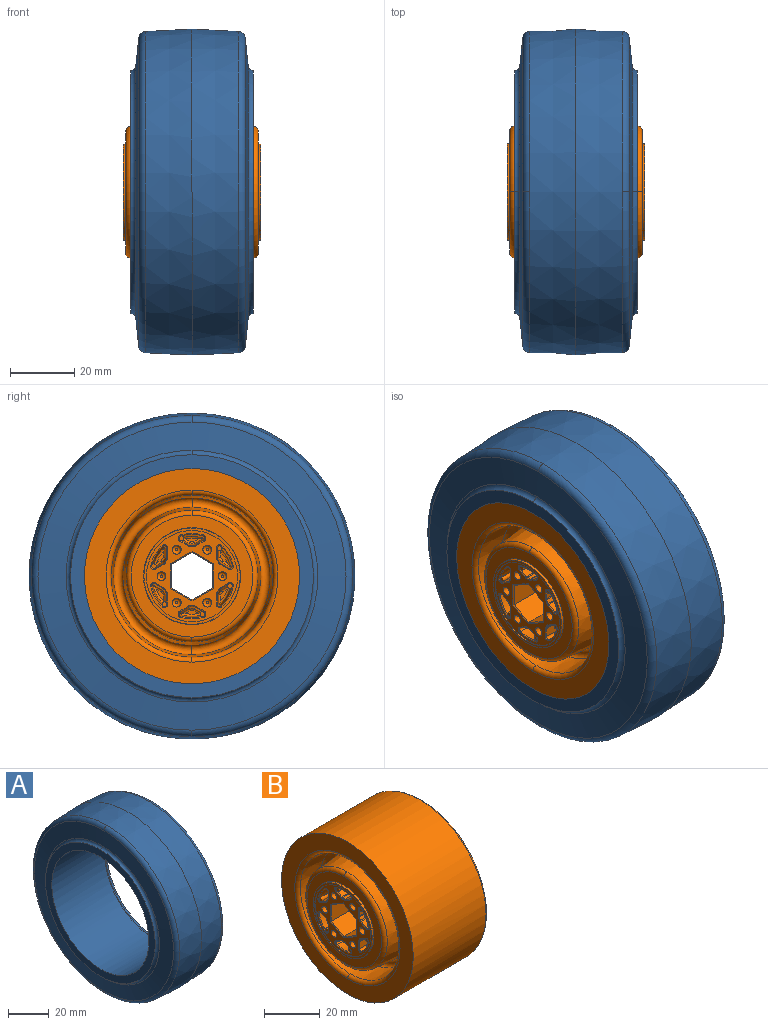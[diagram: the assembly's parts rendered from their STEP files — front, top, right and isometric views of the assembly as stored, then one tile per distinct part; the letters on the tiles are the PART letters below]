
ASSEMBLY  parts=2 mates=1
PART A: 18 faces, bbox 40.3x108.3x108.3 mm
  f0: torus R=47.76mm, axis (-1,0,0), area 500.4mm2, adj f1,f2,f9
  f1: torus R=47.76mm, axis (-1,0,0), area 500.4mm2, adj f0,f2,f9
  f2: cone r=48mm half-angle=84deg, axis (-1,0,0), area 2420.9mm2, adj f0,f1,f3,f4
  f3: torus R=39.37mm, axis (-1,0,0), area 269.1mm2, adj f2,f4,f5
  f4: torus R=39.37mm, axis (-1,0,0), area 269.1mm2, adj f2,f3,f5
  f5: plane 75.69x75.69mm, normal (1,0,0), area 968.2mm2, adj f3,f4,f6
  f6: cone r=33.86mm half-angle=3deg, axis (-1,0,0), area 305mm2, adj f5,f7,f8
  f7: torus R=32.08mm, axis (-1,0,0), area 43.2mm2, adj f6,f8,f17
  f8: torus R=32.08mm, axis (-1,0,0), area 43.2mm2, adj f6,f7,f17
  f9: cone r=50.8mm half-angle=3deg, axis (-1,0,0), area 4586.3mm2, adj f0,f1,f10
  f10: cone r=50.8mm half-angle=3deg, axis (1,0,0), area 4586.3mm2, adj f9,f11,f12
  f11: torus R=47.76mm, axis (-1,0,0), area 500.4mm2, adj f10,f12,f13
  f12: torus R=47.76mm, axis (-1,0,0), area 500.4mm2, adj f10,f11,f13
  f13: cone r=48mm half-angle=84deg, axis (1,0,0), area 2420.9mm2, adj f11,f12,f14,f15
  f14: torus R=39.37mm, axis (-1,0,0), area 269.1mm2, adj f13,f15,f16
  f15: torus R=39.37mm, axis (-1,0,0), area 269.1mm2, adj f13,f14,f16
  f16: plane 75.69x75.69mm, normal (-1,0,0), area 968.2mm2, adj f14,f15,f17
  f17: cylinder r=33.53mm len=67.06mm, axis (1,0,0), area 7806.5mm2, adj f7,f8,f16
PART B: 401 faces, bbox 44.4x74.2x74.2 mm
  f0: torus R=32.08mm, axis (-1,0,0), area 197mm2, adj f2,f57,f400
  f1: plane 67.06x67.06mm, normal (-1,0,0), area 1275.7mm2, adj f10,f56,f400
  f2: torus R=32.08mm, axis (-1,0,0), area 197mm2, adj f0,f57,f400
  f3: revolved ~0.32x0.17mm, area 0.1mm2, adj f41,f43,f102,f103
  f4: revolved ~0.32x0.17mm, area 0.1mm2, adj f42,f48,f86,f87
  f5: torus R=18.98mm, axis (-1,0,0), area 141.5mm2, adj f44,f49,f51
  f6: torus R=18.98mm, axis (-1,0,0), area 141.5mm2, adj f45,f50,f52
  f7: torus R=22.96mm, axis (-1,0,0), area 326.1mm2, adj f44,f46,f53
  f8: torus R=22.96mm, axis (-1,0,0), area 326.1mm2, adj f45,f47,f54
  f9: torus R=26.8mm, axis (-1,0,0), area 183.7mm2, adj f46,f55,f57
  f10: torus R=26.8mm, axis (-1,0,0), area 183.7mm2, adj f1,f47,f56
  f11: cone r=14.2mm half-angle=0.5deg, axis (1,0,0), area 26.8mm2, adj f118,f119
  f12: cylinder r=1.38mm len=18.65mm, axis (1,0,0), area 161.1mm2, adj f19,f119
  f13: cylinder r=1.38mm len=18.65mm, axis (1,0,0), area 161.1mm2, adj f20,f119
  f14: cylinder r=1.38mm len=18.65mm, axis (1,0,0), area 161.1mm2, adj f21,f119
  f15: cylinder r=1.38mm len=18.65mm, axis (1,0,0), area 161.1mm2, adj f22,f119
  f16: cylinder r=1.38mm len=18.65mm, axis (1,0,0), area 161.1mm2, adj f23,f119
  f17: cylinder r=1.38mm len=18.65mm, axis (1,0,0), area 161.1mm2, adj f24,f119
  f18: cone r=13.01mm half-angle=1.5deg, axis (1,0,0), area 128.2mm2, adj f121,f174,f175,f209
  f19: torus R=0.38mm, axis (1,0,0), area 10mm2, adj f12,f239
  f20: torus R=0.38mm, axis (1,0,0), area 10mm2, adj f13,f240
  f21: torus R=0.38mm, axis (1,0,0), area 10mm2, adj f14,f241
  f22: torus R=0.38mm, axis (1,0,0), area 10mm2, adj f15,f242
  f23: torus R=0.38mm, axis (1,0,0), area 10mm2, adj f16,f243
  f24: torus R=0.38mm, axis (1,0,0), area 10mm2, adj f17,f244
  f25: cone r=10.06mm half-angle=1.5deg, axis (-1,0,0), area 23.4mm2, adj f149,f225,f228,f262
  f26: cone r=14.2mm half-angle=0.5deg, axis (-1,0,0), area 26.8mm2, adj f251,f269
  f27: cylinder r=1.38mm len=18.65mm, axis (-1,0,0), area 161.1mm2, adj f34,f269
  f28: cylinder r=1.38mm len=18.65mm, axis (-1,0,0), area 161.1mm2, adj f35,f269
  f29: cylinder r=1.38mm len=18.65mm, axis (-1,0,0), area 161.1mm2, adj f36,f269
  f30: cylinder r=1.38mm len=18.65mm, axis (-1,0,0), area 161.1mm2, adj f37,f269
  f31: cylinder r=1.38mm len=18.65mm, axis (-1,0,0), area 161.1mm2, adj f38,f269
  f32: cylinder r=1.38mm len=18.65mm, axis (-1,0,0), area 161.1mm2, adj f39,f269
  f33: cone r=13.01mm half-angle=1.5deg, axis (-1,0,0), area 128.2mm2, adj f311,f343,f344,f372
  f34: torus R=0.38mm, axis (-1,0,0), area 10mm2, adj f27,f377
  f35: torus R=0.38mm, axis (-1,0,0), area 10mm2, adj f28,f378
  f36: torus R=0.38mm, axis (-1,0,0), area 10mm2, adj f29,f379
  f37: torus R=0.38mm, axis (-1,0,0), area 10mm2, adj f30,f380
  f38: torus R=0.38mm, axis (-1,0,0), area 10mm2, adj f31,f381
  f39: torus R=0.38mm, axis (-1,0,0), area 10mm2, adj f32,f382
  f40: cone r=10.06mm half-angle=1.5deg, axis (1,0,0), area 23.4mm2, adj f293,f357,f360,f389
  f41: cone r=15.17mm half-angle=0.5deg, axis (-1,0,0), area 1115.7mm2, adj f3,f43,f88,f89,f90,f91,f92,f93
  f42: cone r=15.17mm half-angle=0.5deg, axis (1,0,0), area 1115.7mm2, adj f4,f48,f58,f59,f60,f61,f62,f63
  f43: cylinder r=15.11mm len=30.21mm, axis (-1,0,0), area 1052.5mm2, adj f3,f41,f49,f88,f89,f90,f91,f92
  f44: cone r=21.44mm half-angle=5deg, axis (-1,0,0), area 1421mm2, adj f5,f7,f51,f53
  f45: cone r=21.44mm half-angle=5deg, axis (1,0,0), area 1421mm2, adj f6,f8,f52,f54
  f46: cone r=25.28mm half-angle=5deg, axis (1,0,0), area 1436.6mm2, adj f7,f9,f53,f55
  f47: cone r=25.28mm half-angle=5deg, axis (-1,0,0), area 1436.6mm2, adj f8,f10,f54,f56
  f48: cylinder r=15.11mm len=30.21mm, axis (-1,0,0), area 1052.4mm2, adj f4,f42,f50,f58,f59,f60,f61,f62
  f49: plane 37.97x37.97mm, normal (1,0,0), area 415.1mm2, adj f5,f43,f51
  f50: plane 37.97x37.97mm, normal (-1,0,0), area 415.1mm2, adj f6,f48,f52
  f51: torus R=18.98mm, axis (-1,0,0), area 141.5mm2, adj f5,f44,f49
  f52: torus R=18.98mm, axis (-1,0,0), area 141.5mm2, adj f6,f45,f50
  f53: torus R=22.96mm, axis (-1,0,0), area 326.1mm2, adj f7,f44,f46
  f54: torus R=22.96mm, axis (-1,0,0), area 326.1mm2, adj f8,f45,f47
  f55: torus R=26.8mm, axis (-1,0,0), area 183.7mm2, adj f9,f46,f57
  f56: torus R=26.8mm, axis (-1,0,0), area 183.7mm2, adj f1,f10,f47
  f57: plane 64.16x64.16mm, normal (1,0,0), area 977.6mm2, adj f0,f2,f9,f55
  f58: torus R=15.35mm, axis (-1,0,0), area 0.1mm2, adj f42,f48,f59,f83
  f59: bspline ~0.78x0.62mm, area 0.2mm2, adj f42,f48,f58,f82
  f60: torus R=15.35mm, axis (-1,0,0), area 0.1mm2, adj f42,f48,f61,f70
  f61: bspline ~0.78x0.62mm, area 0.2mm2, adj f42,f48,f60,f69
  f62: bspline ~0.78x0.71mm, area 0.1mm2, adj f42,f48,f63,f87
  f63: extruded ~5.58x0.2mm, area 0.6mm2, adj f42,f48,f62
  f64: extruded ~5.58x0.17mm, area 0.6mm2, adj f42,f48,f65
  f65: bspline ~0.78x0.6mm, area 0.2mm2, adj f42,f48,f64,f66
  f66: torus R=15.35mm, axis (-1,0,0), area 0.1mm2, adj f42,f48,f65,f67
  f67: bspline ~0.78x0.63mm, area 0.1mm2, adj f42,f48,f66,f68
  f68: extruded ~5.58x0.18mm, area 0.6mm2, adj f42,f48,f67
  f69: extruded ~5.58x0.18mm, area 0.6mm2, adj f42,f48,f61
  f70: bspline ~0.78x0.6mm, area 0.1mm2, adj f42,f48,f60,f71
  f71: extruded ~5.58x0.17mm, area 0.6mm2, adj f42,f48,f70
  f72: extruded ~5.58x0.2mm, area 0.6mm2, adj f42,f48,f73
  f73: bspline ~0.78x0.71mm, area 0.2mm2, adj f42,f48,f72,f74
  f74: torus R=15.35mm, axis (-1,0,0), area 0.1mm2, adj f42,f48,f73,f75
  f75: bspline ~0.78x0.71mm, area 0.1mm2, adj f42,f48,f74,f76
  f76: extruded ~5.58x0.2mm, area 0.6mm2, adj f42,f48,f75
  f77: extruded ~5.58x0.17mm, area 0.6mm2, adj f42,f48,f78
  f78: bspline ~0.78x0.6mm, area 0.2mm2, adj f42,f48,f77,f79
  f79: torus R=15.35mm, axis (-1,0,0), area 0.1mm2, adj f42,f48,f78,f80
  f80: bspline ~0.78x0.63mm, area 0.2mm2, adj f42,f48,f79,f81
  f81: extruded ~5.58x0.18mm, area 0.6mm2, adj f42,f48,f80
  f82: extruded ~5.58x0.18mm, area 0.6mm2, adj f42,f48,f59
  f83: bspline ~0.78x0.6mm, area 0.1mm2, adj f42,f48,f58,f84
  f84: extruded ~5.58x0.17mm, area 0.6mm2, adj f42,f48,f83
  f85: extruded ~5.58x0.2mm, area 0.6mm2, adj f42,f48,f86
  f86: bspline ~0.78x0.71mm, area 0.2mm2, adj f4,f42,f48,f85
  f87: revolved ~0.32x0.17mm, area 0.1mm2, adj f4,f42,f48,f62
  f88: bspline ~0.78x0.71mm, area 0.1mm2, adj f41,f43,f89,f117
  f89: extruded ~5.58x0.2mm, area 0.6mm2, adj f41,f43,f88
  f90: extruded ~5.58x0.17mm, area 0.6mm2, adj f41,f43,f91
  f91: bspline ~0.78x0.6mm, area 0.2mm2, adj f41,f43,f90,f92
  f92: revolved ~0.59x0.37mm, area 0.1mm2, adj f41,f43,f91,f93
  f93: bspline ~0.78x0.63mm, area 0.2mm2, adj f41,f43,f92,f94
  f94: extruded ~5.58x0.18mm, area 0.6mm2, adj f41,f43,f93
  f95: extruded ~5.58x0.18mm, area 0.6mm2, adj f41,f43,f96
  f96: bspline ~0.78x0.62mm, area 0.2mm2, adj f41,f43,f95,f97
  f97: torus R=15.35mm, axis (-1,0,0), area 0.1mm2, adj f41,f43,f96,f98
  f98: bspline ~0.78x0.6mm, area 0.1mm2, adj f41,f43,f97,f99
  f99: extruded ~5.58x0.17mm, area 0.6mm2, adj f41,f43,f98
  f100: extruded ~5.58x0.2mm, area 0.6mm2, adj f41,f43,f101
  f101: bspline ~0.78x0.71mm, area 0.2mm2, adj f41,f43,f100,f102
  f102: revolved ~0.32x0.17mm, area 0.1mm2, adj f3,f41,f43,f101
  f103: bspline ~0.78x0.71mm, area 0.1mm2, adj f3,f41,f43,f104
  f104: extruded ~5.58x0.2mm, area 0.6mm2, adj f41,f43,f103
  f105: extruded ~5.58x0.17mm, area 0.6mm2, adj f41,f43,f106
  f106: bspline ~0.78x0.6mm, area 0.2mm2, adj f41,f43,f105,f107
  f107: torus R=15.35mm, axis (-1,0,0), area 0.1mm2, adj f41,f43,f106,f108
  f108: bspline ~0.78x0.63mm, area 0.1mm2, adj f41,f43,f107,f109
  f109: extruded ~5.58x0.18mm, area 0.6mm2, adj f41,f43,f108
  f110: extruded ~5.58x0.18mm, area 0.6mm2, adj f41,f43,f111
  f111: bspline ~0.78x0.63mm, area 0.2mm2, adj f41,f43,f110,f112
  f112: torus R=15.35mm, axis (-1,0,0), area 0.1mm2, adj f41,f43,f111,f113
  f113: bspline ~0.78x0.6mm, area 0.1mm2, adj f41,f43,f112,f114
  f114: extruded ~5.58x0.17mm, area 0.6mm2, adj f41,f43,f113
  f115: extruded ~5.58x0.2mm, area 0.6mm2, adj f41,f43,f116
  f116: bspline ~0.78x0.71mm, area 0.2mm2, adj f41,f43,f115,f117
  f117: torus R=15.35mm, axis (-1,0,0), area 0.1mm2, adj f41,f43,f88,f116
  f118: plane 29.99x29.99mm, normal (1,0,0), area 72.9mm2, adj f11,f41
  f119: plane 28.52x28.52mm, normal (1,0,0), area 288.3mm2, adj f11,f12,f13,f14,f15,f16,f17,f120
  f120: bspline ~2.05x0.93mm, area 1mm2, adj f119,f121,f127,f174
  f121: torus R=13.31mm, axis (1,0,0), area 3.3mm2, adj f18,f119,f120,f122
  f122: bspline ~2.04x0.95mm, area 1mm2, adj f119,f121,f123,f175
  f123: cylinder r=0.3mm len=2.75mm, axis (0,0.87,-0.5), area 1.4mm2, adj f119,f122,f124,f176
  f124: bspline ~0.74x0.49mm, area 0.3mm2, adj f119,f123,f125,f210
  f125: torus R=9.28mm, axis (1,0,0), area 0.6mm2, adj f119,f124,f126,f253
  f126: bspline ~0.72x0.49mm, area 0.3mm2, adj f119,f125,f127,f213
  f127: cylinder r=0.3mm len=2.75mm, axis (0,0.87,0.5), area 1.4mm2, adj f119,f120,f126,f177
  f128: bspline ~1.72x1.42mm, area 1mm2, adj f119,f129,f135,f178
  f129: torus R=13.31mm, axis (1,0,0), area 3.3mm2, adj f119,f128,f130,f179
  f130: bspline ~1.92x1.14mm, area 1mm2, adj f119,f129,f131,f180
  f131: cylinder r=0.3mm len=3mm, axis (0,0,-1), area 1.4mm2, adj f119,f130,f132,f181
  f132: bspline ~0.73x0.52mm, area 0.3mm2, adj f119,f131,f133,f215
  f133: torus R=9.28mm, axis (1,0,0), area 0.6mm2, adj f119,f132,f134,f256
  f134: bspline ~0.7x0.68mm, area 0.3mm2, adj f119,f133,f135,f218
  f135: cylinder r=0.3mm len=2.75mm, axis (0,0.87,-0.5), area 1.4mm2, adj f119,f128,f134,f182
  f136: bspline ~1.9x1.15mm, area 1mm2, adj f119,f137,f143,f183
  f137: torus R=13.31mm, axis (1,0,0), area 3.3mm2, adj f119,f136,f138,f184
  f138: bspline ~1.69x1.45mm, area 1mm2, adj f119,f137,f139,f185
  f139: cylinder r=0.3mm len=2.75mm, axis (0,-0.87,-0.5), area 1.4mm2, adj f119,f138,f140,f186
  f140: bspline ~0.7x0.68mm, area 0.3mm2, adj f119,f139,f141,f220
  f141: torus R=9.28mm, axis (1,0,0), area 0.6mm2, adj f119,f140,f142,f259
  f142: bspline ~0.73x0.51mm, area 0.3mm2, adj f119,f141,f143,f223
  f143: cylinder r=0.3mm len=3mm, axis (0,0,-1), area 1.4mm2, adj f119,f136,f142,f187
  f144: bspline ~2.05x0.93mm, area 1mm2, adj f119,f145,f151,f188
  f145: torus R=13.31mm, axis (1,0,0), area 3.3mm2, adj f119,f144,f146,f189
  f146: bspline ~2.04x0.95mm, area 1mm2, adj f119,f145,f147,f190
  f147: cylinder r=0.3mm len=2.75mm, axis (0,-0.87,0.5), area 1.4mm2, adj f119,f146,f148,f191
  f148: bspline ~0.74x0.49mm, area 0.3mm2, adj f119,f147,f149,f225
  f149: torus R=9.28mm, axis (1,0,0), area 0.6mm2, adj f25,f119,f148,f150
  f150: bspline ~0.72x0.49mm, area 0.3mm2, adj f119,f149,f151,f228
  f151: cylinder r=0.3mm len=2.75mm, axis (0,-0.87,-0.5), area 1.4mm2, adj f119,f144,f150,f192
  f152: bspline ~1.72x1.42mm, area 1mm2, adj f119,f153,f159,f193
  f153: torus R=13.31mm, axis (1,0,0), area 3.3mm2, adj f119,f152,f154,f194
  f154: bspline ~1.92x1.14mm, area 1mm2, adj f119,f153,f155,f195
  f155: cylinder r=0.3mm len=3mm, axis (0,0,1), area 1.4mm2, adj f119,f154,f156,f196
  f156: bspline ~0.73x0.52mm, area 0.3mm2, adj f119,f155,f157,f230
  f157: torus R=9.28mm, axis (1,0,0), area 0.6mm2, adj f119,f156,f158,f264
  f158: bspline ~0.7x0.68mm, area 0.3mm2, adj f119,f157,f159,f233
  f159: cylinder r=0.3mm len=2.75mm, axis (0,-0.87,0.5), area 1.4mm2, adj f119,f152,f158,f197
  f160: bspline ~1.9x1.15mm, area 1mm2, adj f119,f161,f167,f198
  f161: torus R=13.31mm, axis (1,0,0), area 3.3mm2, adj f119,f160,f162,f199
  f162: bspline ~1.69x1.45mm, area 1mm2, adj f119,f161,f163,f200
  f163: cylinder r=0.3mm len=2.75mm, axis (0,0.87,0.5), area 1.4mm2, adj f119,f162,f164,f201
  f164: bspline ~0.7x0.68mm, area 0.3mm2, adj f119,f163,f165,f235
  f165: torus R=9.28mm, axis (1,0,0), area 0.6mm2, adj f119,f164,f166,f267
  f166: bspline ~0.73x0.51mm, area 0.3mm2, adj f119,f165,f167,f238
  f167: cylinder r=0.3mm len=3mm, axis (0,0,1), area 1.4mm2, adj f119,f160,f166,f202
  f168: plane 6.66x4.02mm, normal (0.71,0.35,-0.61), area 3.2mm2, adj f119,f169,f173,f203
  f169: plane 7.69x0.3mm, normal (0.71,0.71,0), area 3.2mm2, adj f119,f168,f170,f204
  f170: plane 6.66x4.02mm, normal (0.71,0.35,0.61), area 3.2mm2, adj f119,f169,f171,f205
  f171: plane 6.66x4.02mm, normal (0.71,-0.35,0.61), area 3.2mm2, adj f119,f170,f172,f206
  f172: plane 7.69x0.3mm, normal (0.71,-0.71,0), area 3.2mm2, adj f119,f171,f173,f207
  f173: plane 6.66x4.02mm, normal (0.71,-0.35,-0.61), area 3.2mm2, adj f119,f168,f172,f208
  f174: revolved ~19.11x1.39mm, area 22.6mm2, adj f18,f120,f177,f209,f212
  f175: revolved ~19.11x1.39mm, area 22.6mm2, adj f18,f122,f176,f209,f211
  f176: plane 18.67x2.84mm, normal (0.03,-0.5,-0.87), area 56mm2, adj f123,f175,f210,f211
  f177: plane 18.67x2.84mm, normal (0.03,0.5,-0.87), area 56mm2, adj f127,f174,f212,f213
  f178: revolved ~19.11x1.14mm, area 22.6mm2, adj f128,f179,f182,f214,f217
  f179: cone r=13.01mm half-angle=1.5deg, axis (1,0,0), area 128.2mm2, adj f129,f178,f180,f214
  f180: revolved ~19.11x1.29mm, area 22.6mm2, adj f130,f179,f181,f214,f216
  f181: plane 18.67x3mm, normal (0.03,-1,0), area 56mm2, adj f131,f180,f215,f216
  f182: plane 18.67x2.84mm, normal (0.03,-0.5,-0.87), area 56mm2, adj f135,f178,f217,f218
  f183: revolved ~19.11x1.29mm, area 22.6mm2, adj f136,f184,f187,f219,f222
  f184: cone r=13.01mm half-angle=1.5deg, axis (1,0,0), area 128.2mm2, adj f137,f183,f185,f219
  f185: revolved ~19.11x1.14mm, area 22.6mm2, adj f138,f184,f186,f219,f221
  f186: plane 18.67x2.84mm, normal (0.03,-0.5,0.87), area 56mm2, adj f139,f185,f220,f221
  f187: plane 18.67x3mm, normal (0.03,-1,0), area 56mm2, adj f143,f183,f222,f223
  f188: revolved ~19.11x1.39mm, area 22.6mm2, adj f144,f189,f192,f224,f227
  f189: cone r=13.01mm half-angle=1.5deg, axis (1,0,0), area 128.2mm2, adj f145,f188,f190,f224
  f190: revolved ~19.11x1.39mm, area 22.6mm2, adj f146,f189,f191,f224,f226
  f191: plane 18.67x2.84mm, normal (0.03,0.5,0.87), area 56mm2, adj f147,f190,f225,f226
  f192: plane 18.67x2.84mm, normal (0.03,-0.5,0.87), area 56mm2, adj f151,f188,f227,f228
  f193: revolved ~19.11x1.14mm, area 22.6mm2, adj f152,f194,f197,f229,f232
  f194: cone r=13.01mm half-angle=1.5deg, axis (1,0,0), area 128.2mm2, adj f153,f193,f195,f229
  f195: revolved ~19.11x1.29mm, area 22.6mm2, adj f154,f194,f196,f229,f231
  f196: plane 18.67x3mm, normal (0.03,1,0), area 56mm2, adj f155,f195,f230,f231
  f197: plane 18.67x2.84mm, normal (0.03,0.5,0.87), area 56mm2, adj f159,f193,f232,f233
  f198: revolved ~19.11x1.29mm, area 22.6mm2, adj f160,f199,f202,f234,f237
  f199: cone r=13.01mm half-angle=1.5deg, axis (1,0,0), area 128.2mm2, adj f161,f198,f200,f234
  f200: revolved ~19.11x1.14mm, area 22.6mm2, adj f162,f199,f201,f234,f236
  f201: plane 18.67x2.84mm, normal (0.03,0.5,-0.87), area 56mm2, adj f163,f200,f235,f236
  f202: plane 18.67x3mm, normal (0.03,1,0), area 56mm2, adj f167,f198,f237,f238
  f203: plane 41.69x6.36mm, normal (0,0.5,-0.87), area 306.3mm2, adj f168,f204,f208,f245
  f204: plane 41.69x7.35mm, normal (0,1,0), area 306.3mm2, adj f169,f203,f205,f246
  f205: plane 41.69x6.36mm, normal (0,0.5,0.87), area 306.3mm2, adj f170,f204,f206,f247
  f206: plane 41.69x6.36mm, normal (0,-0.5,0.87), area 306.3mm2, adj f171,f205,f207,f248
  f207: plane 41.69x7.35mm, normal (0,-1,0), area 306.3mm2, adj f172,f206,f208,f249
  f208: plane 41.69x6.36mm, normal (0,-0.5,-0.87), area 306.3mm2, adj f173,f203,f207,f250
  f209: torus R=11.82mm, axis (1,0,0), area 6.7mm2, adj f18,f174,f175,f211,f212,f252
  f210: bspline ~19.55x0.57mm, area 5.6mm2, adj f124,f176,f211,f253,f254
  f211: cylinder r=0.7mm len=3.22mm, axis (0,0.87,-0.5), area 3.1mm2, adj f175,f176,f209,f210,f252,f254
  f212: cylinder r=0.7mm len=3.22mm, axis (0,0.87,0.5), area 3.1mm2, adj f174,f177,f209,f213,f252,f254
  f213: bspline ~19.55x0.57mm, area 5.6mm2, adj f126,f177,f212,f253,f254
  f214: torus R=11.82mm, axis (1,0,0), area 6.7mm2, adj f178,f179,f180,f216,f217,f255
  f215: bspline ~19.55x0.57mm, area 5.6mm2, adj f132,f181,f216,f256,f257
  f216: cylinder r=0.7mm len=3.31mm, axis (0,0,-1), area 3.1mm2, adj f180,f181,f214,f215,f255,f257
  f217: cylinder r=0.7mm len=3.22mm, axis (0,0.87,-0.5), area 3.1mm2, adj f178,f182,f214,f218,f255,f257
  f218: bspline ~19.55x0.59mm, area 5.6mm2, adj f134,f182,f217,f256,f257
  f219: torus R=11.82mm, axis (1,0,0), area 6.7mm2, adj f183,f184,f185,f221,f222,f258
  f220: bspline ~19.55x0.59mm, area 5.6mm2, adj f140,f186,f221,f259,f260
  f221: cylinder r=0.7mm len=3.22mm, axis (0,-0.87,-0.5), area 3.1mm2, adj f185,f186,f219,f220,f258,f260
  f222: cylinder r=0.7mm len=3.31mm, axis (0,0,-1), area 3.1mm2, adj f183,f187,f219,f223,f258,f260
  f223: bspline ~19.55x0.57mm, area 5.6mm2, adj f142,f187,f222,f259,f260
  f224: torus R=11.82mm, axis (1,0,0), area 6.7mm2, adj f188,f189,f190,f226,f227,f261
  f225: bspline ~19.55x0.57mm, area 5.6mm2, adj f25,f148,f191,f226,f262
  f226: cylinder r=0.7mm len=3.22mm, axis (0,-0.87,0.5), area 3.1mm2, adj f190,f191,f224,f225,f261,f262
  f227: cylinder r=0.7mm len=3.22mm, axis (0,-0.87,-0.5), area 3.1mm2, adj f188,f192,f224,f228,f261,f262
  f228: bspline ~19.55x0.57mm, area 5.6mm2, adj f25,f150,f192,f227,f262
  f229: torus R=11.82mm, axis (1,0,0), area 6.7mm2, adj f193,f194,f195,f231,f232,f263
  f230: bspline ~19.55x0.57mm, area 5.6mm2, adj f156,f196,f231,f264,f265
  f231: cylinder r=0.7mm len=3.31mm, axis (0,0,1), area 3.1mm2, adj f195,f196,f229,f230,f263,f265
  f232: cylinder r=0.7mm len=3.22mm, axis (0,-0.87,0.5), area 3.1mm2, adj f193,f197,f229,f233,f263,f265
  f233: bspline ~19.55x0.59mm, area 5.6mm2, adj f158,f197,f232,f264,f265
  f234: torus R=11.82mm, axis (1,0,0), area 6.7mm2, adj f198,f199,f200,f236,f237,f266
  f235: bspline ~19.55x0.59mm, area 5.6mm2, adj f164,f201,f236,f267,f268
  f236: cylinder r=0.7mm len=3.22mm, axis (0,0.87,0.5), area 3.1mm2, adj f200,f201,f234,f235,f266,f268
  f237: cylinder r=0.7mm len=3.31mm, axis (0,0,1), area 3.1mm2, adj f198,f202,f234,f238,f266,f268
  f238: bspline ~19.55x0.57mm, area 5.6mm2, adj f166,f202,f237,f267,f268
  f239: plane 0.75x0.75mm, normal (1,0,0), area 0.4mm2, adj f19
  f240: plane 0.75x0.75mm, normal (1,0,0), area 0.4mm2, adj f20
  f241: plane 0.75x0.75mm, normal (1,0,0), area 0.4mm2, adj f21
  f242: plane 0.75x0.75mm, normal (1,0,0), area 0.4mm2, adj f22
  f243: plane 0.75x0.75mm, normal (1,0,0), area 0.4mm2, adj f23
  f244: plane 0.75x0.75mm, normal (1,0,0), area 0.4mm2, adj f24
  f245: plane 6.66x4.02mm, normal (-0.71,0.35,-0.61), area 3.2mm2, adj f203,f246,f250,f269
  f246: plane 7.69x0.3mm, normal (-0.71,0.71,0), area 3.2mm2, adj f204,f245,f247,f269
  f247: plane 6.66x4.02mm, normal (-0.71,0.35,0.61), area 3.2mm2, adj f205,f246,f248,f269
  f248: plane 6.66x4.02mm, normal (-0.71,-0.35,0.61), area 3.2mm2, adj f206,f247,f249,f269
  f249: plane 7.69x0.3mm, normal (-0.71,-0.71,0), area 3.2mm2, adj f207,f248,f250,f269
  f250: plane 6.66x4.02mm, normal (-0.71,-0.35,-0.61), area 3.2mm2, adj f208,f245,f249,f269
  f251: plane 29.99x29.99mm, normal (-1,0,0), area 72.9mm2, adj f26,f42
  f252: plane 4.17x1.07mm, normal (1,0,0), area 2.8mm2, adj f209,f211,f212,f254
  f253: cone r=10.06mm half-angle=1.5deg, axis (-1,0,0), area 23.4mm2, adj f125,f210,f213,f254
  f254: torus R=10.76mm, axis (1,0,0), area 1.4mm2, adj f210,f211,f212,f213,f252,f253
  f255: plane 3.61x2.08mm, normal (1,0,0), area 2.8mm2, adj f214,f216,f217,f257
  f256: cone r=10.06mm half-angle=1.5deg, axis (-1,0,0), area 23.4mm2, adj f133,f215,f218,f257
  f257: torus R=10.76mm, axis (1,0,0), area 1.4mm2, adj f215,f216,f217,f218,f255,f256
  f258: plane 3.61x2.08mm, normal (1,0,0), area 2.8mm2, adj f219,f221,f222,f260
  f259: cone r=10.06mm half-angle=1.5deg, axis (-1,0,0), area 23.4mm2, adj f141,f220,f223,f260
  f260: torus R=10.76mm, axis (1,0,0), area 1.4mm2, adj f220,f221,f222,f223,f258,f259
  f261: plane 4.17x1.07mm, normal (1,0,0), area 2.8mm2, adj f224,f226,f227,f262
  f262: torus R=10.76mm, axis (1,0,0), area 1.4mm2, adj f25,f225,f226,f227,f228,f261
  f263: plane 3.61x2.08mm, normal (1,0,0), area 2.8mm2, adj f229,f231,f232,f265
  f264: cone r=10.06mm half-angle=1.5deg, axis (-1,0,0), area 23.4mm2, adj f157,f230,f233,f265
  f265: torus R=10.76mm, axis (1,0,0), area 1.4mm2, adj f230,f231,f232,f233,f263,f264
  f266: plane 3.61x2.08mm, normal (1,0,0), area 2.8mm2, adj f234,f236,f237,f268
  f267: cone r=10.06mm half-angle=1.5deg, axis (-1,0,0), area 23.4mm2, adj f165,f235,f238,f268
  f268: torus R=10.76mm, axis (1,0,0), area 1.4mm2, adj f235,f236,f237,f238,f266,f267
  f269: plane 28.49x28.49mm, normal (-1,0,0), area 288.3mm2, adj f26,f27,f28,f29,f30,f31,f32,f245
  f270: bspline ~0.68x0.68mm, area 0.3mm2, adj f269,f271,f277,f347
  f271: cylinder r=0.3mm len=2.75mm, axis (0,0.87,0.5), area 1.4mm2, adj f269,f270,f272,f318
  f272: bspline ~1.72x1.42mm, area 1.1mm2, adj f269,f271,f273,f319
  f273: torus R=13.31mm, axis (-1,0,0), area 3.3mm2, adj f269,f272,f274,f320
  f274: bspline ~1.92x1.15mm, area 1.1mm2, adj f269,f273,f275,f321
  f275: cylinder r=0.3mm len=3mm, axis (0,0,1), area 1.4mm2, adj f269,f274,f276,f322
  f276: bspline ~0.69x0.51mm, area 0.3mm2, adj f269,f275,f277,f350
  f277: torus R=9.28mm, axis (-1,0,0), area 0.6mm2, adj f269,f270,f276,f383
  f278: bspline ~0.71x0.52mm, area 0.3mm2, adj f269,f279,f285,f352
  f279: cylinder r=0.3mm len=3mm, axis (0,0,1), area 1.4mm2, adj f269,f278,f280,f323
  f280: bspline ~1.91x1.18mm, area 1.1mm2, adj f269,f279,f281,f324
  f281: torus R=13.31mm, axis (-1,0,0), area 3.3mm2, adj f269,f280,f282,f325
  f282: bspline ~1.69x1.45mm, area 1.1mm2, adj f269,f281,f283,f326
  f283: cylinder r=0.3mm len=2.75mm, axis (0,-0.87,0.5), area 1.4mm2, adj f269,f282,f284,f327
  f284: bspline ~0.7x0.68mm, area 0.3mm2, adj f269,f283,f285,f355
  f285: torus R=9.28mm, axis (-1,0,0), area 0.6mm2, adj f269,f278,f284,f386
  f286: bspline ~0.72x0.49mm, area 0.3mm2, adj f269,f287,f293,f357
  f287: cylinder r=0.3mm len=2.75mm, axis (0,-0.87,0.5), area 1.4mm2, adj f269,f286,f288,f328
  f288: bspline ~2.06x0.94mm, area 1.1mm2, adj f269,f287,f289,f329
  f289: torus R=13.31mm, axis (-1,0,0), area 3.3mm2, adj f269,f288,f290,f330
  f290: bspline ~2.05x0.95mm, area 1.1mm2, adj f269,f289,f291,f331
  f291: cylinder r=0.3mm len=2.75mm, axis (0,-0.87,-0.5), area 1.4mm2, adj f269,f290,f292,f332
  f292: bspline ~0.7x0.48mm, area 0.3mm2, adj f269,f291,f293,f360
  f293: torus R=9.28mm, axis (-1,0,0), area 0.6mm2, adj f40,f269,f286,f292
  f294: bspline ~0.69x0.51mm, area 0.3mm2, adj f269,f295,f301,f365
  f295: torus R=9.28mm, axis (-1,0,0), area 0.6mm2, adj f269,f294,f296,f391
  f296: bspline ~0.68x0.68mm, area 0.3mm2, adj f269,f295,f297,f362
  f297: cylinder r=0.3mm len=2.75mm, axis (0,-0.87,-0.5), area 1.4mm2, adj f269,f296,f298,f333
  f298: bspline ~1.72x1.42mm, area 1.1mm2, adj f269,f297,f299,f334
  f299: torus R=13.31mm, axis (-1,0,0), area 3.3mm2, adj f269,f298,f300,f335
  f300: bspline ~1.92x1.15mm, area 1.1mm2, adj f269,f299,f301,f336
  f301: cylinder r=0.3mm len=3mm, axis (0,0,-1), area 1.4mm2, adj f269,f294,f300,f337
  f302: bspline ~0.71x0.52mm, area 0.3mm2, adj f269,f303,f309,f367
  f303: cylinder r=0.3mm len=3mm, axis (0,0,-1), area 1.4mm2, adj f269,f302,f304,f338
  f304: bspline ~1.91x1.18mm, area 1.1mm2, adj f269,f303,f305,f339
  f305: torus R=13.31mm, axis (-1,0,0), area 3.3mm2, adj f269,f304,f306,f340
  f306: bspline ~1.69x1.45mm, area 1.1mm2, adj f269,f305,f307,f341
  f307: cylinder r=0.3mm len=2.75mm, axis (0,0.87,-0.5), area 1.4mm2, adj f269,f306,f308,f342
  f308: bspline ~0.7x0.68mm, area 0.3mm2, adj f269,f307,f309,f370
  f309: torus R=9.28mm, axis (-1,0,0), area 0.6mm2, adj f269,f302,f308,f394
  f310: bspline ~2.06x0.94mm, area 1.1mm2, adj f269,f311,f317,f343
  f311: torus R=13.31mm, axis (-1,0,0), area 3.3mm2, adj f33,f269,f310,f312
  f312: bspline ~2.05x0.95mm, area 1.1mm2, adj f269,f311,f313,f344
  f313: cylinder r=0.3mm len=2.75mm, axis (0,0.87,0.5), area 1.4mm2, adj f269,f312,f314,f345
  f314: bspline ~0.7x0.48mm, area 0.3mm2, adj f269,f313,f315,f373
  f315: torus R=9.28mm, axis (-1,0,0), area 0.6mm2, adj f269,f314,f316,f399
  f316: bspline ~0.72x0.49mm, area 0.3mm2, adj f269,f315,f317,f375
  f317: cylinder r=0.3mm len=2.75mm, axis (0,0.87,-0.5), area 1.4mm2, adj f269,f310,f316,f346
  f318: plane 18.67x2.84mm, normal (-0.03,-0.5,0.87), area 56mm2, adj f271,f319,f347,f348
  f319: revolved ~19.11x1.13mm, area 22.6mm2, adj f272,f318,f320,f348,f349
  f320: cone r=13.01mm half-angle=1.5deg, axis (-1,0,0), area 128.2mm2, adj f273,f319,f321,f349
  f321: revolved ~19.11x1.51mm, area 52.8mm2, adj f274,f320,f322,f349,f351
  f322: plane 20.17x4.5mm, normal (-0.03,-1,0), area 56mm2, adj f275,f321,f350,f351
  f323: plane 18.67x3mm, normal (-0.03,-1,0), area 56mm2, adj f279,f324,f352,f353
  f324: revolved ~19.11x1.29mm, area 22.6mm2, adj f280,f323,f325,f353,f354
  f325: cone r=13.01mm half-angle=1.5deg, axis (-1,0,0), area 128.2mm2, adj f281,f324,f326,f354
  f326: revolved ~19.11x1.51mm, area 52.8mm2, adj f282,f325,f327,f354,f356
  f327: plane 20.17x4.34mm, normal (-0.03,-0.5,-0.87), area 56mm2, adj f283,f326,f355,f356
  f328: plane 18.67x2.84mm, normal (-0.03,-0.5,-0.87), area 56mm2, adj f287,f329,f357,f358
  f329: revolved ~19.11x1.38mm, area 22.6mm2, adj f288,f328,f330,f358,f359
  f330: cone r=13.01mm half-angle=1.5deg, axis (-1,0,0), area 128.2mm2, adj f289,f329,f331,f359
  f331: revolved ~19.11x1.51mm, area 52.8mm2, adj f290,f330,f332,f359,f361
  f332: plane 20.17x4.34mm, normal (-0.03,0.5,-0.87), area 56mm2, adj f291,f331,f360,f361
  f333: plane 18.67x2.84mm, normal (-0.03,0.5,-0.87), area 56mm2, adj f297,f334,f362,f363
  f334: revolved ~19.11x1.13mm, area 22.6mm2, adj f298,f333,f335,f363,f364
  f335: cone r=13.01mm half-angle=1.5deg, axis (-1,0,0), area 128.2mm2, adj f299,f334,f336,f364
  f336: revolved ~19.11x1.51mm, area 52.8mm2, adj f300,f335,f337,f364,f366
  f337: plane 20.17x4.5mm, normal (-0.03,1,0), area 56mm2, adj f301,f336,f365,f366
  f338: plane 18.67x3mm, normal (-0.03,1,0), area 56mm2, adj f303,f339,f367,f368
  f339: revolved ~19.11x1.29mm, area 22.6mm2, adj f304,f338,f340,f368,f369
  f340: cone r=13.01mm half-angle=1.5deg, axis (-1,0,0), area 128.2mm2, adj f305,f339,f341,f369
  f341: revolved ~19.11x1.51mm, area 52.8mm2, adj f306,f340,f342,f369,f371
  f342: plane 20.17x4.34mm, normal (-0.03,0.5,0.87), area 56mm2, adj f307,f341,f370,f371
  f343: revolved ~19.11x1.38mm, area 22.6mm2, adj f33,f310,f346,f372,f376
  f344: revolved ~19.11x1.51mm, area 52.8mm2, adj f33,f312,f345,f372,f374
  f345: plane 20.17x4.34mm, normal (-0.03,-0.5,0.87), area 56mm2, adj f313,f344,f373,f374
  f346: plane 18.67x2.84mm, normal (-0.03,0.5,0.87), area 56mm2, adj f317,f343,f375,f376
  f347: bspline ~19.55x0.59mm, area 5.6mm2, adj f270,f318,f348,f383,f384
  f348: cylinder r=0.7mm len=3.22mm, axis (0,0.87,0.5), area 3.1mm2, adj f318,f319,f347,f349,f384,f385
  f349: torus R=11.82mm, axis (-1,0,0), area 6.7mm2, adj f319,f320,f321,f348,f351,f385
  f350: bspline ~19.55x0.57mm, area 5.6mm2, adj f276,f322,f351,f383,f384
  f351: cylinder r=0.7mm len=3.31mm, axis (0,0,1), area 3.1mm2, adj f321,f322,f349,f350,f384,f385
  f352: bspline ~19.55x0.57mm, area 5.6mm2, adj f278,f323,f353,f386,f387
  f353: cylinder r=0.7mm len=3.31mm, axis (0,0,1), area 3.1mm2, adj f323,f324,f352,f354,f387,f388
  f354: torus R=11.82mm, axis (-1,0,0), area 6.7mm2, adj f324,f325,f326,f353,f356,f388
  f355: bspline ~19.55x0.59mm, area 5.6mm2, adj f284,f327,f356,f386,f387
  f356: cylinder r=0.7mm len=3.22mm, axis (0,-0.87,0.5), area 3.1mm2, adj f326,f327,f354,f355,f387,f388
  f357: bspline ~19.55x0.57mm, area 5.6mm2, adj f40,f286,f328,f358,f389
  f358: cylinder r=0.7mm len=3.22mm, axis (0,-0.87,0.5), area 3.1mm2, adj f328,f329,f357,f359,f389,f390
  f359: torus R=11.82mm, axis (-1,0,0), area 6.7mm2, adj f329,f330,f331,f358,f361,f390
  f360: bspline ~19.55x0.57mm, area 5.6mm2, adj f40,f292,f332,f361,f389
  f361: cylinder r=0.7mm len=3.22mm, axis (0,-0.87,-0.5), area 3.1mm2, adj f331,f332,f359,f360,f389,f390
  f362: bspline ~19.55x0.59mm, area 5.6mm2, adj f296,f333,f363,f391,f392
  f363: cylinder r=0.7mm len=3.22mm, axis (0,-0.87,-0.5), area 3.1mm2, adj f333,f334,f362,f364,f392,f393
  f364: torus R=11.82mm, axis (-1,0,0), area 6.7mm2, adj f334,f335,f336,f363,f366,f393
  f365: bspline ~19.55x0.57mm, area 5.6mm2, adj f294,f337,f366,f391,f392
  f366: cylinder r=0.7mm len=3.31mm, axis (0,0,-1), area 3.1mm2, adj f336,f337,f364,f365,f392,f393
  f367: bspline ~19.55x0.57mm, area 5.6mm2, adj f302,f338,f368,f394,f395
  f368: cylinder r=0.7mm len=3.31mm, axis (0,0,-1), area 3.1mm2, adj f338,f339,f367,f369,f395,f396
  f369: torus R=11.82mm, axis (-1,0,0), area 6.7mm2, adj f339,f340,f341,f368,f371,f396
  f370: bspline ~19.55x0.59mm, area 5.6mm2, adj f308,f342,f371,f394,f395
  f371: cylinder r=0.7mm len=3.22mm, axis (0,0.87,-0.5), area 3.1mm2, adj f341,f342,f369,f370,f395,f396
  f372: torus R=11.82mm, axis (-1,0,0), area 6.7mm2, adj f33,f343,f344,f374,f376,f397
  f373: bspline ~19.55x0.57mm, area 5.6mm2, adj f314,f345,f374,f398,f399
  f374: cylinder r=0.7mm len=3.22mm, axis (0,0.87,0.5), area 3.1mm2, adj f344,f345,f372,f373,f397,f398
  f375: bspline ~19.55x0.57mm, area 5.6mm2, adj f316,f346,f376,f398,f399
  f376: cylinder r=0.7mm len=3.22mm, axis (0,0.87,-0.5), area 3.1mm2, adj f343,f346,f372,f375,f397,f398
  f377: plane 0.75x0.75mm, normal (-1,0,0), area 0.4mm2, adj f34
  f378: plane 0.75x0.75mm, normal (-1,0,0), area 0.4mm2, adj f35
  f379: plane 0.75x0.75mm, normal (-1,0,0), area 0.4mm2, adj f36
  f380: plane 0.75x0.75mm, normal (-1,0,0), area 0.4mm2, adj f37
  f381: plane 0.75x0.75mm, normal (-1,0,0), area 0.4mm2, adj f38
  f382: plane 0.75x0.75mm, normal (-1,0,0), area 0.4mm2, adj f39
  f383: cone r=10.06mm half-angle=1.5deg, axis (1,0,0), area 23.4mm2, adj f277,f347,f350,f384
  f384: torus R=10.76mm, axis (-1,0,0), area 1.4mm2, adj f347,f348,f350,f351,f383,f385
  f385: plane 3.61x2.08mm, normal (-1,0,0), area 2.8mm2, adj f348,f349,f351,f384
  f386: cone r=10.06mm half-angle=1.5deg, axis (1,0,0), area 23.4mm2, adj f285,f352,f355,f387
  f387: torus R=10.76mm, axis (-1,0,0), area 1.4mm2, adj f352,f353,f355,f356,f386,f388
  f388: plane 3.61x2.08mm, normal (-1,0,0), area 2.8mm2, adj f353,f354,f356,f387
  f389: torus R=10.76mm, axis (-1,0,0), area 1.4mm2, adj f40,f357,f358,f360,f361,f390
  f390: plane 4.17x1.07mm, normal (-1,0,0), area 2.8mm2, adj f358,f359,f361,f389
  f391: cone r=10.06mm half-angle=1.5deg, axis (1,0,0), area 23.4mm2, adj f295,f362,f365,f392
  f392: torus R=10.76mm, axis (-1,0,0), area 1.4mm2, adj f362,f363,f365,f366,f391,f393
  f393: plane 3.61x2.08mm, normal (-1,0,0), area 2.8mm2, adj f363,f364,f366,f392
  f394: cone r=10.06mm half-angle=1.5deg, axis (1,0,0), area 23.4mm2, adj f309,f367,f370,f395
  f395: torus R=10.76mm, axis (-1,0,0), area 1.4mm2, adj f367,f368,f370,f371,f394,f396
  f396: plane 3.61x2.08mm, normal (-1,0,0), area 2.8mm2, adj f368,f369,f371,f395
  f397: plane 4.17x1.07mm, normal (-1,0,0), area 2.8mm2, adj f372,f374,f376,f398
  f398: torus R=10.76mm, axis (-1,0,0), area 1.4mm2, adj f373,f374,f375,f376,f397,f399
  f399: cone r=10.06mm half-angle=1.5deg, axis (1,0,0), area 23.4mm2, adj f315,f373,f375,f398
  f400: cylinder r=33.53mm len=67.06mm, axis (1,0,0), area 7806.5mm2, adj f0,f1,f2
PLACE A t=(-21.15,0,0)mm
PLACE B t=(-21.15,0,0)mm
MATE fastened A.f2 <-> B.f11  axis (1,0,0) through (-21.67,0,0)mm
